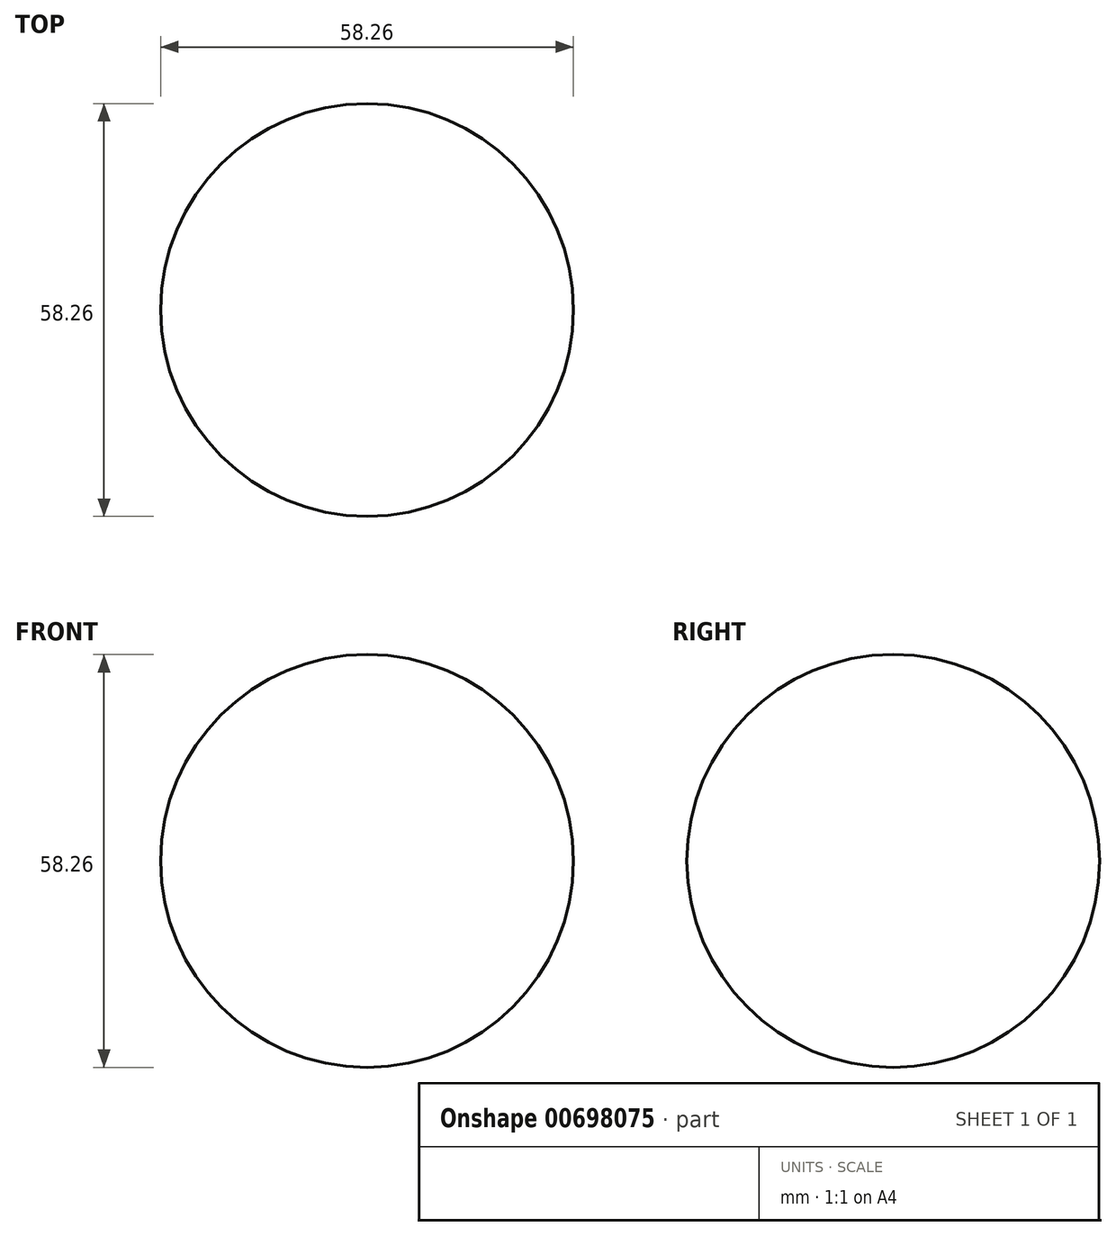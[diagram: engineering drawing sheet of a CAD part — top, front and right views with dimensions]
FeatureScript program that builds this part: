
annotation { "Feature Type Name" : "Feature", "Feature Type Description" : "" }
export const myFeature = defineFeature(function(context is Context, id is Id, definition is map)
    precondition{}
    {
        {
            var Q0;
            Q0=qCreatedBy(makeId("Front.planeOp"),FACE);
            var sketch = newSketch(context, id + "F0", { "sketchPlane" : qUnion([Q0])});
            skCircle(sketch, "E0", {"center": v(0, 0) * mm, "radius": 29.13 * mm});
            skLineSegment(sketch, "E1", {"start": v(0, 0) * mm, "end": v(56.06, 0) * mm});
            skLineSegment(sketch, "E2", {"start": v(56.06, 0) * mm, "end": v(-46.74, 0) * mm});
            skSolve(sketch);
        }
        {
            var Q0;
            {var subQ0=sQuery(id+"F0.wireOp",EDGE,"E2");var subQ4=makeQuery(id+"F0.imprint","IMPRINT",VERTEX,{"derivedFrom":subQ0});Q0=makeQuery(id+"F0.imprint","IMPRINT",FACE,{"disambiguationData":[TD([[makeQuery(id+"F0.imprint","IMPRINT",EDGE,{"disambiguationData":[TD([[subQ4,1.0]])],"derivedFrom":subQ0}),-1.0]])]});}
            var Q1;
            Q1=sQuery(id+"F0.wireOp",EDGE,"E2");
            revolve(context, id + "F1", {"entities" : qUnion([Q0]), "axis" : qUnion([Q1]), "revolveType" : RevolveType.FULL, "surfaceOperationType" : NewSurfaceOperationType.NEW});
        }
    });
